# Revit family: Haworth_Planes_ConferenceTable_HexagonOnePiece
name_source: partatom
category: Furniture Systems
revit_build: Autodesk Revit 2018 (Build: 20170223_1515(x64)
units: mm (PartAtom-declared; Revit-internal decimal feet)

## family parameters
Always vertical = Yes
Cut with Voids When Loaded = No
OmniClass Number = 23.40.70.14.64.21
OmniClass Title = Systems Furniture
Part Type = Normal
Room Calculation Point = No
Round Connector Dimension = Use Diameter
Shared = No
Work Plane-Based = No

## types (45) — shared parameters
Actual Height = 29"
Assembly Code = E2020200
Cable Base = Yes
Cube Base Finish = Haworth _ Laminate _ Maple H-AE
Description = Haworth - Planes - Conference Table - Hexagon One Piece
Flip Top - Double Sided = No
Flip Top - Double Sided Wide = No
Flip Top - Single Sided = Yes
Flip Top - Single Sided Wide = No
Flip Top Center = Yes
Flip Top Finish = Haworth _ Paint _ Metallic Champagne
Flip Top Left/Right = No
Manufacturer = Haworth
Max. Height = 29"
Middle Leg Off_Override = No
Middle Leg_Interior = No
Min. Height = 29"
Min/Max Width = 72-120 @ 6 in. increments
Model = Haworth - Planes - Conference Table - Hexagon One Piece
Revision Number = 2
Size = Verify Final Dim. w/ Haworth
Standard Depths = 36, 42, 48, 54, 60 in.
Standard Height = 29 in.
Support Finish = Haworth _ Paint _ Metallic Champagne
Support Height = 27 13/16"
Support Location_Side = 10"
Support Middle Offset = 5"
Sustainability Info = http://www.haworth.com
Table Thickness = 1 3/16"
URL = www.haworth.com
URL - Product = http://www.haworth.com
Warranty = http://www.haworth.com
Worksurface Edge Finish = Haworth _ Laminate _ Maple H-AE
Worksurface Finish = Haworth _ Laminate _ Maple H-AE

## per-type parameters (varying)
| type | Actual Depth | Actual Width | Cable Base 14 x 14 | Custom Size | Depth | Flip Top Position | Max. Depth | Max. Width | Min. Depth | Min. Width | Standard 36 | Standard 42 | Support Location_Front_Back | Width |
| 72w 36d | 36" | 72" | No | No | 36" | 18" | 36" | 96" | 36" | 72" | Yes | No | 8" | 72" |
| 78w 36d | 36" | 78" | No | No | 36" | 19 1/2" | 36" | 96" | 36" | 72" | Yes | No | 8" | 78" |
| 84w 36d | 36" | 84" | No | No | 36" | 21" | 60" | 96" | 36" | 72" | Yes | No | 8" | 84" |
| 90w 36d | 36" | 90" | No | No | 36" | 22 1/2" | 60" | 96" | 36" | 72" | Yes | No | 8" | 90" |
| 96w 36d | 36" | 96" | No | No | 36" | 24" | 60" | 96" | 36" | 72" | Yes | No | 8" | 96" |
| 102w 36d | 42" | 96" | Yes | Yes | 36" | 24" | 60" | 96" | 42" | 72" | No | No | 8" | 102" |
| 108w 36d | 42" | 96" | Yes | Yes | 36" | 24" | 60" | 96" | 42" | 72" | No | No | 8" | 108" |
| 114w 36d | 42" | 96" | Yes | Yes | 36" | 24" | 60" | 96" | 42" | 72" | No | No | 8" | 114" |
| 120w 36d | 42" | 96" | Yes | Yes | 36" | 24" | 60" | 96" | 42" | 72" | No | No | 8" | 120" |
| 72 42d | 36" | 84" | No | Yes | 42" | 21" | 36" | 120" | 36" | 84" | No | No | 8" | 72" |
| 78 42d | 36" | 84" | No | Yes | 42" | 21" | 36" | 120" | 36" | 84" | No | No | 8" | 78" |
| 84 42d | 42" | 84" | Yes | No | 42" | 21" | 60" | 120" | 36" | 84" | No | Yes | 8" | 84" |
| 90 42d | 42" | 90" | Yes | No | 42" | 22 1/2" | 60" | 120" | 36" | 84" | No | Yes | 8" | 90" |
| 96 42d | 42" | 96" | Yes | No | 42" | 24" | 60" | 120" | 36" | 84" | No | Yes | 8" | 96" |
| 102 42d | 42" | 102" | Yes | No | 42" | 25 1/2" | 60" | 120" | 42" | 84" | No | Yes | 8" | 102" |
| 108 42d | 42" | 108" | Yes | No | 42" | 27" | 60" | 120" | 42" | 84" | No | Yes | 8" | 108" |
| 114 42d | 42" | 114" | Yes | No | 42" | 28 1/2" | 60" | 120" | 42" | 84" | No | Yes | 8" | 114" |
| 120 42d | 42" | 120" | Yes | No | 42" | 30" | 60" | 120" | 42" | 84" | No | Yes | 8" | 120" |
| 72 48d | 36" | 84" | No | Yes | 48" | 21" | 36" | 120" | 36" | 84" | No | No | 8" | 72" |
| 78w 48d | 36" | 84" | No | Yes | 48" | 21" | 36" | 120" | 36" | 84" | No | No | 8" | 78" |
| 84w 48d | 48" | 84" | Yes | No | 48" | 21" | 60" | 120" | 36" | 84" | No | Yes | 10" | 84" |
| 90w 48d | 48" | 90" | Yes | No | 48" | 22 1/2" | 60" | 120" | 36" | 84" | No | Yes | 10" | 90" |
| 96w 48d | 48" | 96" | Yes | No | 48" | 24" | 60" | 120" | 36" | 84" | No | Yes | 10" | 96" |
| 102w 48d | 48" | 102" | Yes | No | 48" | 25 1/2" | 60" | 120" | 42" | 84" | No | Yes | 10" | 102" |
| 108w 48d | 48" | 108" | Yes | No | 48" | 27" | 60" | 120" | 42" | 84" | No | Yes | 10" | 108" |
| 114w 48d | 48" | 114" | Yes | No | 48" | 28 1/2" | 60" | 120" | 42" | 84" | No | Yes | 10" | 114" |
| 120w 48d | 48" | 120" | Yes | No | 48" | 30" | 60" | 120" | 42" | 84" | No | Yes | 10" | 120" |
| 72w 54d | 36" | 84" | No | Yes | 54" | 21" | 36" | 120" | 36" | 84" | No | No | 8" | 72" |
| 78w 54d | 36" | 84" | No | Yes | 54" | 21" | 36" | 120" | 36" | 84" | No | No | 8" | 78" |
| 84w 54d | 54" | 84" | Yes | No | 54" | 21" | 60" | 120" | 36" | 84" | No | Yes | 10" | 84" |
| 90w 54d | 54" | 90" | Yes | No | 54" | 22 1/2" | 60" | 120" | 36" | 84" | No | Yes | 10" | 90" |
| 96w 54d | 54" | 96" | Yes | No | 54" | 24" | 60" | 120" | 36" | 84" | No | Yes | 10" | 96" |
| 102w 54d | 54" | 102" | Yes | No | 54" | 25 1/2" | 60" | 120" | 42" | 84" | No | Yes | 10" | 102" |
| 108 54d | 54" | 108" | Yes | No | 54" | 27" | 60" | 120" | 42" | 84" | No | Yes | 10" | 108" |
| 114 54d | 54" | 114" | Yes | No | 54" | 28 1/2" | 60" | 120" | 42" | 84" | No | Yes | 10" | 114" |
| 120 54d | 54" | 120" | Yes | No | 54" | 30" | 60" | 120" | 42" | 84" | No | Yes | 10" | 120" |
| 72 60d | 36" | 84" | No | Yes | 60" | 21" | 36" | 120" | 36" | 84" | No | No | 8" | 72" |
| 78 60d | 36" | 84" | No | Yes | 60" | 21" | 36" | 120" | 36" | 84" | No | No | 8" | 78" |
| 84 60d | 60" | 84" | Yes | No | 60" | 21" | 60" | 120" | 36" | 84" | No | Yes | 10" | 84" |
| 90 60d | 60" | 90" | Yes | No | 60" | 22 1/2" | 60" | 120" | 36" | 84" | No | Yes | 10" | 90" |
| 96 60d | 60" | 96" | Yes | No | 60" | 24" | 60" | 120" | 36" | 84" | No | Yes | 10" | 96" |
| 102 60d | 60" | 102" | Yes | No | 60" | 25 1/2" | 60" | 120" | 42" | 84" | No | Yes | 10" | 102" |
| 108 60d | 60" | 108" | Yes | No | 60" | 27" | 60" | 120" | 42" | 84" | No | Yes | 10" | 108" |
| 114 60d | 60" | 114" | Yes | No | 60" | 28 1/2" | 60" | 120" | 42" | 84" | No | Yes | 10" | 114" |
| 120 60d | 60" | 120" | Yes | No | 60" | 30" | 60" | 120" | 42" | 84" | No | Yes | 10" | 120" |

## geometry (parser evidence)
native form markers: Sweep x14
no freeform markers — native parametric forms only
